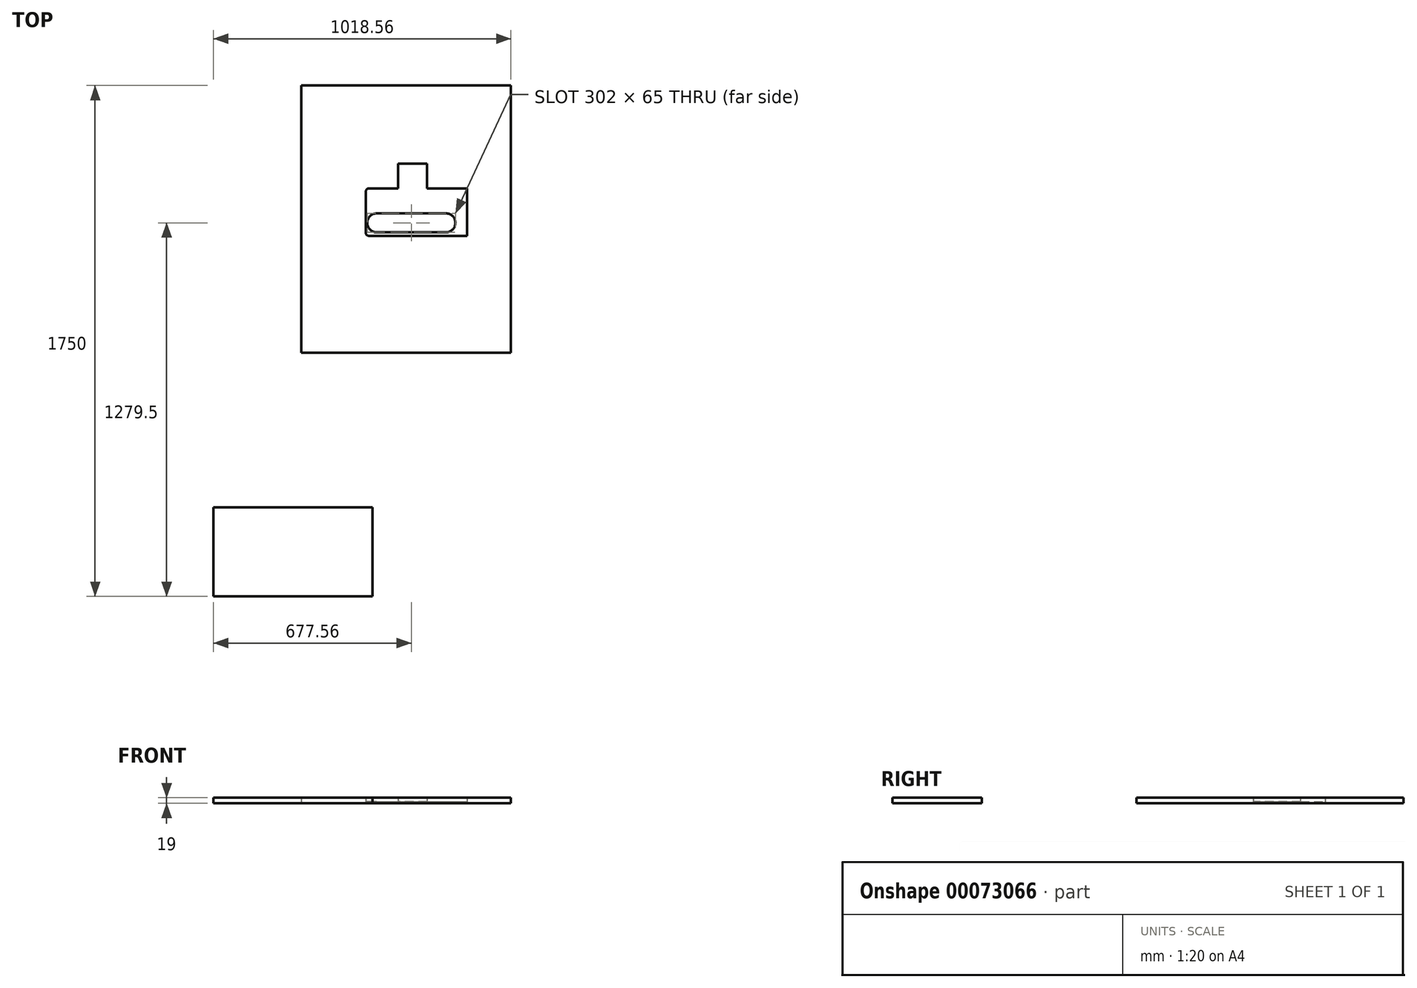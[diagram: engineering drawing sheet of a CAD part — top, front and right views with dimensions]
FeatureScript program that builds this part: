
annotation { "Feature Type Name" : "Feature", "Feature Type Description" : "" }
export const myFeature = defineFeature(function(context is Context, id is Id, definition is map)
    precondition{}
    {
        {
            var Q0;
            Q0=qCreatedBy(makeId("Top.planeOp"),FACE);
            var sketch = newSketch(context, id + "F5", { "sketchPlane" : qUnion([Q0])});
            skLineSegment(sketch, "E0.bottom", {"start": v(0, 915) * mm, "end": v(718, 915) * mm});
            skLineSegment(sketch, "E0.top", {"start": v(0, 0) * mm, "end": v(718, 0) * mm});
            skLineSegment(sketch, "E0.left", {"start": v(0, 915) * mm, "end": v(0, 0) * mm});
            skLineSegment(sketch, "E0.right", {"start": v(718, 915) * mm, "end": v(718, 0) * mm});
            skLineSegment(sketch, "E1.bottom", {"start": v(-300.56, -530.2) * mm, "end": v(244.44, -530.2) * mm});
            skLineSegment(sketch, "E1.top", {"start": v(-300.56, -835) * mm, "end": v(244.44, -835) * mm});
            skLineSegment(sketch, "E1.left", {"start": v(-300.56, -530.2) * mm, "end": v(-300.56, -835) * mm});
            skLineSegment(sketch, "E1.right", {"start": v(244.44, -530.2) * mm, "end": v(244.44, -835) * mm});
            skSolve(sketch);
        }
        {
            var Q0;
            Q0=makeQuery(id+"F5.imprint","IMPRINT",FACE,{"disambiguationData":[TD([[makeQuery(id+"F5.imprint","IMPRINT",EDGE,{"derivedFrom":sQuery(id+"F5.wireOp",EDGE,"E0.bottom")}),-1.0]])]});
            var sketch = newSketch(context, id + "F0", { "sketchPlane" : qUnion([Q0])});
            skLineSegment(sketch, "E2.1", {"start": v(228, 444.5) * mm, "end": v(228, 444.5) * mm});
            skLineSegment(sketch, "E2.2", {"start": v(258.5, 475) * mm, "end": v(495.5, 475) * mm});
            skLineSegment(sketch, "E2.5", {"start": v(526, 444.5) * mm, "end": v(526, 444.5) * mm});
            skPoint(sketch, "E3.visualSharp", {"position": v(221, 400) * mm});
            skLineSegment(sketch, "E2.7", {"start": v(258.5, 414) * mm, "end": v(495.5, 414) * mm});
            skPoint(sketch, "E4.visualSharp", {"position": v(221, 562) * mm});
            skPoint(sketch, "E5.visualSharp", {"position": v(226, 477) * mm});
            skLineSegment(sketch, "E6.2", {"start": v(231, 402) * mm, "end": v(568, 402) * mm});
            skLineSegment(sketch, "E7", {"start": v(231, 400) * mm, "end": v(568, 400) * mm});
            skLineSegment(sketch, "E8", {"start": v(221, 410) * mm, "end": v(221, 552) * mm});
            skLineSegment(sketch, "E9", {"start": v(231, 562) * mm, "end": v(568, 562) * mm});
            skLineSegment(sketch, "E10", {"start": v(568, 562) * mm, "end": v(568, 400) * mm});
            skPoint(sketch, "E11.visualSharp", {"position": v(528, 477) * mm});
            skLineSegment(sketch, "E12.0", {"start": v(258.5, 412) * mm, "end": v(495.5, 412) * mm});
            skLineSegment(sketch, "E13.0", {"start": v(226, 444.5) * mm, "end": v(226, 444.5) * mm});
            skLineSegment(sketch, "E14.0", {"start": v(258.5, 477) * mm, "end": v(495.5, 477) * mm});
            skLineSegment(sketch, "E15", {"start": v(528, 444.5) * mm, "end": v(528, 444.5) * mm});
            skLineSegment(sketch, "E6.3", {"start": v(231, 560) * mm, "end": v(568, 560) * mm});
            skPoint(sketch, "E16.visualSharp", {"position": v(528, 412) * mm});
            skLineSegment(sketch, "E6.5", {"start": v(223, 410) * mm, "end": v(223, 552) * mm});
            skPoint(sketch, "E17.visualSharp", {"position": v(226, 412) * mm});
            skArc(sketch, "E3.filletArc", {"start": v(221, 410) * mm, "mid": v(223.93, 402.93) * mm, "end": v(231, 400) * mm});
            skArc(sketch, "E6.4", {"start": v(223, 410) * mm, "mid": v(225.34, 404.34) * mm, "end": v(231, 402) * mm});
            skArc(sketch, "E2.6", {"start": v(495.5, 414) * mm, "mid": v(517.07, 422.93) * mm, "end": v(526, 444.5) * mm});
            skArc(sketch, "E16.filletArc", {"start": v(495.5, 412) * mm, "mid": v(518.48, 421.52) * mm, "end": v(528, 444.5) * mm});
            skArc(sketch, "E6.0", {"start": v(231, 560) * mm, "mid": v(225.34, 557.66) * mm, "end": v(223, 552) * mm});
            skArc(sketch, "E4.filletArc", {"start": v(231, 562) * mm, "mid": v(223.93, 559.07) * mm, "end": v(221, 552) * mm});
            skArc(sketch, "E5.filletArc", {"start": v(258.5, 477) * mm, "mid": v(235.52, 467.48) * mm, "end": v(226, 444.5) * mm});
            skArc(sketch, "E11.filletArc", {"start": v(528, 444.5) * mm, "mid": v(518.48, 467.48) * mm, "end": v(495.5, 477) * mm});
            skArc(sketch, "E2.0", {"start": v(258.5, 475) * mm, "mid": v(236.93, 466.07) * mm, "end": v(228, 444.5) * mm});
            skArc(sketch, "E2.4", {"start": v(526, 444.5) * mm, "mid": v(517.07, 466.07) * mm, "end": v(495.5, 475) * mm});
            skArc(sketch, "E17.filletArc", {"start": v(226, 444.5) * mm, "mid": v(235.52, 421.52) * mm, "end": v(258.5, 412) * mm});
            skArc(sketch, "E2.3", {"start": v(228, 444.5) * mm, "mid": v(236.93, 422.93) * mm, "end": v(258.5, 414) * mm});
            skLineSegment(sketch, "E18", {"start": v(718, 0) * mm, "end": v(718, 915) * mm});
            skLineSegment(sketch, "E19", {"start": v(718, 0) * mm, "end": v(0, 0) * mm});
            skLineSegment(sketch, "E20", {"start": v(431, 562) * mm, "end": v(431, 647) * mm});
            skLineSegment(sketch, "E21", {"start": v(431, 647) * mm, "end": v(331, 647) * mm});
            skLineSegment(sketch, "E22", {"start": v(331, 647) * mm, "end": v(331, 562) * mm});
            skPoint(sketch, "E23", {"position": v(381, 647) * mm});
            skSolve(sketch);
        }
        {
            var Q0;
            Q0 = qSketchRegion(id + "F5", true);
            extrude(context, id + "F1", {"entities" : qUnion([Q0]), "depth" : 19 * mm});
        }
        {
            var Q0;
            {var subQ1=sQuery(id+"F0.wireOp",EDGE,"E6.2");Q0=makeQuery(id+"F0.imprint","IMPRINT",FACE,{"disambiguationData":[TD([[makeQuery(id+"F0.imprint","IMPRINT",EDGE,{"derivedFrom":subQ1}),1.0]])]});}
            var Q1;
            Q1=makeQuery(id+"F0.imprint","IMPRINT",FACE,{"disambiguationData":[TD([[makeQuery(id+"F0.imprint","IMPRINT",EDGE,{"derivedFrom":sQuery(id+"F0.wireOp",EDGE,"E2.2")}),-1.0]])]});
            var Q2;
            Q2=makeQuery(id+"F0.imprint","IMPRINT",FACE,{"disambiguationData":[TD([[makeQuery(id+"F0.imprint","IMPRINT",EDGE,{"derivedFrom":sQuery(id+"F0.wireOp",EDGE,"E2.2")}),1.0]])]});
            var Q3;
            {var subQ2=sQuery(id+"F0.wireOp",EDGE,"E6.2");Q3=makeQuery(id+"F0.imprint","IMPRINT",FACE,{"disambiguationData":[TD([[makeQuery(id+"F0.imprint","IMPRINT",EDGE,{"derivedFrom":subQ2}),-1.0]])]});}
            extrude(context, id + "F2", {"entities" : qUnion([Q0, Q1, Q2, Q3]), "operationType" : NewBodyOperationType.REMOVE, "depth" : 30 * mm});
        }
        {
            var Q0;
            Q0 = qSketchRegion(id + "F0", true);
            extrude(context, id + "F3", {"entities" : qUnion([Q0]), "operationType" : NewBodyOperationType.ADD, "depth" : 5 * mm});
        }
        {
            var Q0;
            {var subQ0=sQuery(id+"F0.wireOp",EDGE,"E20");Q0=makeQuery(id+"F0.imprint","IMPRINT",FACE,{"disambiguationData":[TD([[makeQuery(id+"F0.imprint","IMPRINT",EDGE,{"derivedFrom":subQ0}),1.0]])]});}
            extrude(context, id + "F4", {"entities" : qUnion([Q0]), "operationType" : NewBodyOperationType.REMOVE, "depth" : 45 * mm, "hasSecondDirection" : true, "secondDirectionOppositeDirection" : false, "secondDirectionDepth" : 5 * mm});
        }
    });
